# Revit family: Volleyball_System-PSS-8001R-Ceiling_Hung
name_source: partatom
category: Specialty Equipment
revit_build: Autodesk Revit 2017 (Build: 20170816_0615(x64)
units: mm (PartAtom-declared; Revit-internal decimal feet)

## family parameters
Always vertical = Yes
Cut with Voids When Loaded = No
OmniClass Number = 23.40.50.34.14
OmniClass Title = Gymnasium Equipment
Part Type = Normal
Room Calculation Point = No
Round Connector Dimension = Use Diameter
Shared = No
Work Plane-Based = No

## types (1)
- Volleyball_System-PSS-8001R-Ceiling_Hung
    Assembly Code = E1020900
    BIM Version = v3.1
    CSI MasterFormat = 11 66 23
    Description = Skymaster® with Referee Stand, 1-Court Ceiling-Hung Fold-Up Volleyball System
    Manufacturer = Performance Sports Systems
    Model = 8001R
    Net Height = 7' - 11 5/8"
    Padding Color = Vinyl Padding - Performance Sports Systems - W09 White
    Product Page URL = http://www.perfsports.com
    Superstructure Finish = Powder Coat - Performance Sports Systems - Black
    Sway Brace Height = 15' - 0 7/8"
    URL = http://www.perfsports.com

## geometry (parser evidence)
native form markers: Blend x86, Sweep x28
no freeform markers — native parametric forms only
